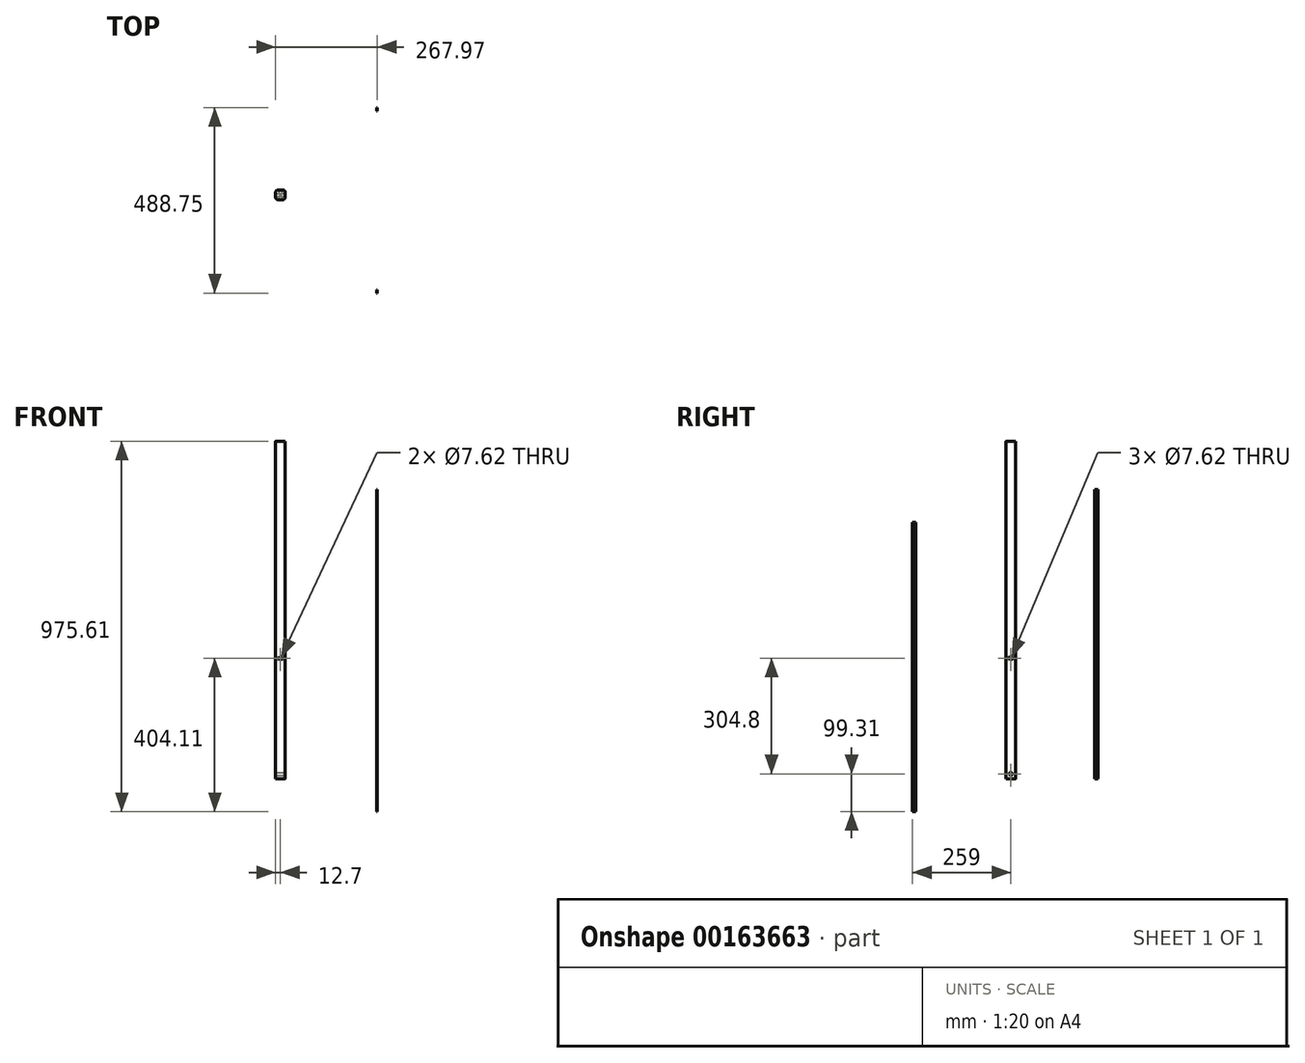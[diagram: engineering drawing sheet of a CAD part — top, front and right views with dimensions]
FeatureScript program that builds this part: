
annotation { "Feature Type Name" : "Feature", "Feature Type Description" : "" }
export const myFeature = defineFeature(function(context is Context, id is Id, definition is map)
    precondition{}
    {
        {
            var Q0;
            Q0=qCreatedBy(makeId("Top.planeOp"),FACE);
            var sketch = newSketch(context, id + "F0", { "sketchPlane" : qUnion([Q0])});
            skLineSegment(sketch, "E0.bottom", {"start": v(6.35, 12.7) * mm, "end": v(-6.35, 12.7) * mm});
            skLineSegment(sketch, "E0.top", {"start": v(6.35, -12.7) * mm, "end": v(-6.35, -12.7) * mm});
            skLineSegment(sketch, "E0.left", {"start": v(12.7, 6.35) * mm, "end": v(12.7, -6.35) * mm});
            skLineSegment(sketch, "E0.right", {"start": v(-12.7, 6.35) * mm, "end": v(-12.7, -6.35) * mm});
            skPoint(sketch, "E0.middle", {"position": v(0, 0) * mm});
            skPoint(sketch, "E1.visualSharp", {"position": v(-12.7, 12.7) * mm});
            skArc(sketch, "E1.filletArc", {"start": v(-6.35, 12.7) * mm, "mid": v(-10.84, 10.84) * mm, "end": v(-12.7, 6.35) * mm});
            skPoint(sketch, "E2.visualSharp", {"position": v(-12.7, -12.7) * mm});
            skArc(sketch, "E2.filletArc", {"start": v(-12.7, -6.35) * mm, "mid": v(-10.84, -10.84) * mm, "end": v(-6.35, -12.7) * mm});
            skPoint(sketch, "E3.visualSharp", {"position": v(12.7, -12.7) * mm});
            skArc(sketch, "E3.filletArc", {"start": v(6.35, -12.7) * mm, "mid": v(10.84, -10.84) * mm, "end": v(12.7, -6.35) * mm});
            skPoint(sketch, "E4.visualSharp", {"position": v(12.7, 12.7) * mm});
            skArc(sketch, "E4.filletArc", {"start": v(12.7, 6.35) * mm, "mid": v(10.84, 10.84) * mm, "end": v(6.35, 12.7) * mm});
            skSolve(sketch);
        }
        {
            var Q0;
            Q0=qSketchRegion(id+"F0",true);
            extrude(context, id + "F1", {"entities" : qUnion([Q0]), "depth" : 889 * mm});
        }
        {
            var Q0;
            Q0=qCreatedBy(makeId("Right.planeOp"),FACE);
            var sketch = newSketch(context, id + "F2", { "sketchPlane" : qUnion([Q0])});
            skLineSegment(sketch, "E5.bottom", {"start": v(-259, 675.39) * mm, "end": v(-250.53, 675.39) * mm});
            skLineSegment(sketch, "E5.top", {"start": v(-259, -86.61) * mm, "end": v(-250.53, -86.61) * mm});
            skLineSegment(sketch, "E5.left", {"start": v(-259, 675.39) * mm, "end": v(-259, -86.61) * mm});
            skLineSegment(sketch, "E5.right", {"start": v(-250.53, 675.39) * mm, "end": v(-250.53, -86.61) * mm});
            skSolve(sketch);
        }
        {
            var Q0;
            Q0=makeQuery(id+"F2.imprint","IMPRINT",FACE,{"disambiguationData":[TD([[makeQuery(id+"F2.imprint","IMPRINT",EDGE,{"derivedFrom":sQuery(id+"F2.wireOp",EDGE,"E5.bottom")}),-1.0]])]});
            extrude(context, id + "F3", {"entities" : qUnion([Q0]), "depth" : 1.27 * mm});
        }
        {
            var Q0;
            Q0=qCreatedBy(makeId("Right.planeOp"),FACE);
            var sketch = newSketch(context, id + "F4", { "sketchPlane" : qUnion([Q0])});
            skLineSegment(sketch, "E6.bottom", {"start": v(221.29, 762) * mm, "end": v(229.75, 762) * mm});
            skLineSegment(sketch, "E6.top", {"start": v(221.29, 0) * mm, "end": v(229.75, 0) * mm});
            skLineSegment(sketch, "E6.left", {"start": v(221.29, 762) * mm, "end": v(221.29, 0) * mm});
            skLineSegment(sketch, "E6.right", {"start": v(229.75, 762) * mm, "end": v(229.75, 0) * mm});
            skSolve(sketch);
        }
        {
            var Q0;
            Q0=makeQuery(id+"F4.imprint","IMPRINT",FACE,{"disambiguationData":[TD([[makeQuery(id+"F4.imprint","IMPRINT",EDGE,{"derivedFrom":sQuery(id+"F4.wireOp",EDGE,"E6.bottom")}),-1.0]])]});
            var Q1;
            Q1=sQuery(id+"F4.wireOp",EDGE,"E6.right");
            var Q2;
            Q2=sQuery(id+"F4.wireOp",EDGE,"E6.left");
            var Q3;
            Q3=sQuery(id+"F4.wireOp",EDGE,"E6.top");
            var Q4;
            Q4=sQuery(id+"F4.wireOp",EDGE,"E6.bottom");
            extrude(context, id + "F5", {"entities" : qUnion([Q0]), "surfaceEntities" : qUnion([Q1, Q2, Q3, Q4]), "depth" : 1.27 * mm});
        }
        {
            var Q0;
            Q0=makeQuery(id+"F1.opExtrude","SWEPT_FACE",FACE,{"disambiguationData":[OSD([sQuery(id+"F0.wireOp",EDGE,"E0.left")])]});
            var sketch = newSketch(context, id + "F6", { "sketchPlane" : qUnion([Q0])});
            skCircle(sketch, "E7", {"center": v(0, 12.7) * mm, "radius": 3.81 * mm});
            skCircle(sketch, "E8", {"center": v(0, 317.5) * mm, "radius": 3.81 * mm});
            skSolve(sketch);
        }
        {
            var Q0;
            Q0=makeQuery(id+"F6.imprint","IMPRINT",FACE,{"disambiguationData":[TD([[makeQuery(id+"F6.imprint","IMPRINT",EDGE,{"derivedFrom":sQuery(id+"F6.wireOp",EDGE,"E7")}),1.0]])]});
            var Q1;
            Q1=makeQuery(id+"F6.imprint","IMPRINT",FACE,{"disambiguationData":[TD([[makeQuery(id+"F6.imprint","IMPRINT",EDGE,{"derivedFrom":sQuery(id+"F6.wireOp",EDGE,"E8")}),1.0]])]});
            extrude(context, id + "F7", {"entities" : qUnion([Q0, Q1]), "operationType" : NewBodyOperationType.REMOVE, "oppositeDirection" : true, "depth" : 25.4 * mm});
        }
        {
            var Q0;
            Q0=makeQuery(id+"F3.opExtrude","SWEPT_BODY",BODY,{"disambiguationData":[OSD([sQuery(id+"F2.wireOp",EDGE,"E5.bottom"),sQuery(id+"F2.wireOp",EDGE,"E5.top"),sQuery(id+"F2.wireOp",EDGE,"E5.left"),sQuery(id+"F2.wireOp",EDGE,"E5.right")])]});
            var Q1;
            Q1=makeQuery(id+"F5.opExtrude","SWEPT_BODY",BODY,{"disambiguationData":[OSD([sQuery(id+"F4.wireOp",EDGE,"E6.bottom"),sQuery(id+"F4.wireOp",EDGE,"E6.top"),sQuery(id+"F4.wireOp",EDGE,"E6.left"),sQuery(id+"F4.wireOp",EDGE,"E6.right")])]});
            transform(context, id + "F8", {"entities" : qUnion([Q0, Q1]), "transformType" : TransformType.TRANSLATION_3D, "dx" : 254 * mm, "dy" : 0 * mm, "dz" : 0 * mm, "makeCopy" : false});
        }
        {
            var Q0;
            Q0=makeQuery(id+"F1.opExtrude","SWEPT_FACE",FACE,{"disambiguationData":[OSD([sQuery(id+"F0.wireOp",EDGE,"E0.top")])]});
            var sketch = newSketch(context, id + "F9", { "sketchPlane" : qUnion([Q0])});
            skLineSegment(sketch, "E9", {"start": v(0, 0) * mm, "end": v(0, 317.5) * mm});
            skCircle(sketch, "E10", {"center": v(0, 317.5) * mm, "radius": 3.81 * mm});
            skSolve(sketch);
        }
        {
            var Q0;
            Q0=makeQuery(id+"F9.imprint","IMPRINT",FACE,{"disambiguationData":[TD([[makeQuery(id+"F9.imprint","IMPRINT",EDGE,{"derivedFrom":sQuery(id+"F9.wireOp",EDGE,"E10")}),1.0]])]});
            extrude(context, id + "F10", {"entities" : qUnion([Q0]), "operationType" : NewBodyOperationType.REMOVE, "oppositeDirection" : true, "depth" : 25.4 * mm});
        }
    });
